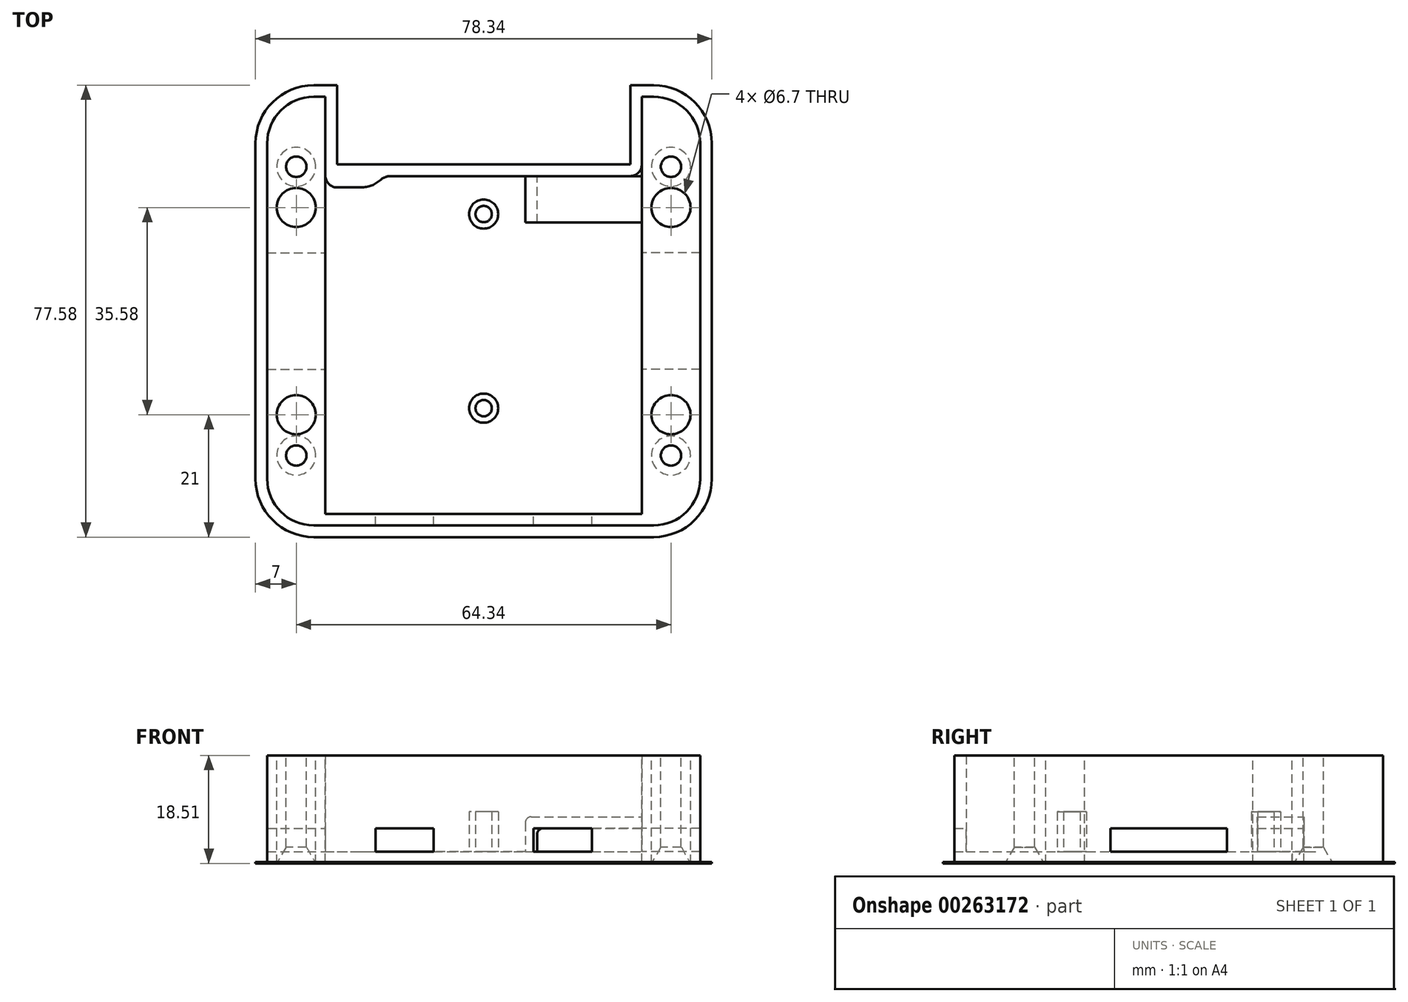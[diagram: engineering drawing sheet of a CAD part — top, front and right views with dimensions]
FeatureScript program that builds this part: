
annotation { "Feature Type Name" : "Feature", "Feature Type Description" : "" }
export const myFeature = defineFeature(function(context is Context, id is Id, definition is map)
    precondition{}
    {
        {
            var Q0;
            Q0=qCreatedBy(makeId("Top.planeOp"),FACE);
            var sketch = newSketch(context, id + "F0", { "sketchPlane" : qUnion([Q0])});
            skLineSegment(sketch, "E0.bottom", {"start": v(8, 0) * mm, "end": v(66.34, 0) * mm, "construction": true});
            skLineSegment(sketch, "E0.top", {"start": v(8, 73.58) * mm, "end": v(66.34, 73.58) * mm, "construction": true});
            skLineSegment(sketch, "E0.left", {"start": v(0, 8) * mm, "end": v(0, 65.58) * mm, "construction": true});
            skLineSegment(sketch, "E0.right", {"start": v(74.34, 8) * mm, "end": v(74.34, 65.58) * mm, "construction": true});
            skArc(sketch, "E1", {"start": v(8, 73.58) * mm, "mid": v(2.34, 71.24) * mm, "end": v(0, 65.58) * mm, "construction": true});
            skArc(sketch, "E2", {"start": v(0, 8) * mm, "mid": v(2.34, 2.34) * mm, "end": v(8, 0) * mm, "construction": true});
            skArc(sketch, "E3", {"start": v(74.34, 65.58) * mm, "mid": v(72, 71.24) * mm, "end": v(66.34, 73.58) * mm, "construction": true});
            skArc(sketch, "E4", {"start": v(66.34, 0) * mm, "mid": v(72, 2.34) * mm, "end": v(74.34, 8) * mm, "construction": true});
            skCircle(sketch, "E5", {"center": v(5, 61.58) * mm, "radius": 1.4 * mm, "construction": true});
            skCircle(sketch, "E6", {"center": v(5, 54.58) * mm, "radius": 3.35 * mm, "construction": true});
            skLineSegment(sketch, "E7", {"start": v(0, 36.8) * mm, "end": v(74.34, 36.8) * mm, "construction": true});
            skLineSegment(sketch, "E8", {"start": v(37.17, 73.58) * mm, "end": v(37.17, 0) * mm, "construction": true});
            skCircle(sketch, "E9.MirrorC", {"center": v(69.34, 54.58) * mm, "radius": 3.35 * mm, "construction": true});
            skCircle(sketch, "E10.MirrorC", {"center": v(69.34, 61.58) * mm, "radius": 1.4 * mm, "construction": true});
            skCircle(sketch, "E11.MirrorC", {"center": v(69.34, 12) * mm, "radius": 1.4 * mm, "construction": true});
            skCircle(sketch, "E12.MirrorC", {"center": v(69.34, 19) * mm, "radius": 3.35 * mm, "construction": true});
            skCircle(sketch, "E13.MirrorC", {"center": v(5, 19) * mm, "radius": 3.35 * mm, "construction": true});
            skCircle(sketch, "E14.MirrorC", {"center": v(5, 12) * mm, "radius": 1.4 * mm, "construction": true});
            skCircle(sketch, "E15", {"center": v(16.14, 63.03) * mm, "radius": 3.3 * mm, "construction": true});
            skLineSegment(sketch, "E16.bottom", {"start": v(10.83, 54.55) * mm, "end": v(15.24, 54.55) * mm, "construction": true});
            skLineSegment(sketch, "E16.top", {"start": v(10.84, 5.31) * mm, "end": v(15.25, 5.31) * mm, "construction": true});
            skLineSegment(sketch, "E16.left", {"start": v(10.83, 54.55) * mm, "end": v(10.83, 5.31) * mm, "construction": true});
            skLineSegment(sketch, "E16.right", {"start": v(15.24, 54.55) * mm, "end": v(15.24, 5.31) * mm, "construction": true});
            skLineSegment(sketch, "E17.bottom", {"start": v(32.84, 69.48) * mm, "end": v(62.84, 69.48) * mm, "construction": true});
            skLineSegment(sketch, "E17.top", {"start": v(32.84, 59.98) * mm, "end": v(62.84, 59.98) * mm, "construction": true});
            skLineSegment(sketch, "E17.left", {"start": v(32.84, 69.48) * mm, "end": v(32.84, 59.98) * mm, "construction": true});
            skLineSegment(sketch, "E17.right", {"start": v(62.84, 69.48) * mm, "end": v(62.84, 59.98) * mm, "construction": true});
            skLineSegment(sketch, "E18.bottom", {"start": v(59.1, 45.4) * mm, "end": v(63.5, 45.4) * mm, "construction": true});
            skLineSegment(sketch, "E18.top", {"start": v(59.1, 5.3) * mm, "end": v(63.5, 5.3) * mm, "construction": true});
            skLineSegment(sketch, "E18.left", {"start": v(59.1, 45.4) * mm, "end": v(59.1, 5.3) * mm, "construction": true});
            skLineSegment(sketch, "E18.right", {"start": v(63.5, 45.4) * mm, "end": v(63.5, 5.3) * mm, "construction": true});
            skLineSegment(sketch, "E19.bottom", {"start": v(19.88, 57) * mm, "end": v(31.88, 57) * mm, "construction": true});
            skLineSegment(sketch, "E19.top", {"start": v(19.88, 41) * mm, "end": v(21.13, 41) * mm, "construction": true});
            skLineSegment(sketch, "E19.left", {"start": v(19.88, 57) * mm, "end": v(19.88, 41) * mm, "construction": true});
            skLineSegment(sketch, "E19.right", {"start": v(31.88, 57) * mm, "end": v(31.88, 41) * mm, "construction": true});
            skLineSegment(sketch, "E20", {"start": v(21.13, 41) * mm, "end": v(21.14, 8.5) * mm, "construction": true});
            skLineSegment(sketch, "E21", {"start": v(21.14, 8.5) * mm, "end": v(30.64, 8.5) * mm, "construction": true});
            skLineSegment(sketch, "E22", {"start": v(30.64, 8.5) * mm, "end": v(30.64, 41) * mm, "construction": true});
            skLineSegment(sketch, "E23.trimOffspring", {"start": v(30.64, 41) * mm, "end": v(31.88, 41) * mm, "construction": true});
            skSolve(sketch);
        }
        {
            var Q0;
            Q0=qCreatedBy(makeId("Top.planeOp"),FACE);
            var sketch = newSketch(context, id + "F1", { "sketchPlane" : qUnion([Q0])});
            skLineSegment(sketch, "E24", {"start": v(0, 65.58) * mm, "end": v(0, 8) * mm});
            skLineSegment(sketch, "E25", {"start": v(74.34, 65.58) * mm, "end": v(74.34, 8) * mm});
            skCircle(sketch, "E26", {"center": v(5, 61.58) * mm, "radius": 1.75 * mm});
            skCircle(sketch, "E27", {"center": v(5, 12) * mm, "radius": 1.75 * mm});
            skCircle(sketch, "E28", {"center": v(69.34, 12) * mm, "radius": 1.75 * mm});
            skCircle(sketch, "E29", {"center": v(69.34, 61.58) * mm, "radius": 1.75 * mm});
            skCircle(sketch, "E30", {"center": v(5, 54.58) * mm, "radius": 3.35 * mm});
            skCircle(sketch, "E31", {"center": v(5, 19) * mm, "radius": 3.35 * mm});
            skCircle(sketch, "E32", {"center": v(69.34, 19) * mm, "radius": 3.35 * mm});
            skCircle(sketch, "E33", {"center": v(69.34, 54.58) * mm, "radius": 3.35 * mm});
            skLineSegment(sketch, "E34", {"start": v(8, 73.58) * mm, "end": v(10, 73.58) * mm});
            skArc(sketch, "E35", {"start": v(8, 73.58) * mm, "mid": v(2.34, 71.24) * mm, "end": v(0, 65.58) * mm});
            skArc(sketch, "E36", {"start": v(74.34, 65.58) * mm, "mid": v(72, 71.24) * mm, "end": v(66.34, 73.58) * mm});
            skLineSegment(sketch, "E37", {"start": v(8, 0) * mm, "end": v(66.34, 0) * mm});
            skArc(sketch, "E38", {"start": v(0, 8) * mm, "mid": v(2.34, 2.34) * mm, "end": v(8, 0) * mm});
            skArc(sketch, "E39", {"start": v(66.34, 0) * mm, "mid": v(72, 2.34) * mm, "end": v(74.34, 8) * mm});
            skArc(sketch, "E40", {"start": v(16.14, 58.03) * mm, "mid": v(17.94, 58.37) * mm, "end": v(19.5, 59.33) * mm});
            skLineSegment(sketch, "E41", {"start": v(64.34, 59.98) * mm, "end": v(21.18, 59.98) * mm});
            skArc(sketch, "E42", {"start": v(21.18, 59.98) * mm, "mid": v(20.28, 59.81) * mm, "end": v(19.5, 59.33) * mm});
            skLineSegment(sketch, "E43", {"start": v(64.34, 59.98) * mm, "end": v(64.34, 73.58) * mm});
            skLineSegment(sketch, "E44", {"start": v(66.34, 73.58) * mm, "end": v(64.34, 73.58) * mm});
            skLineSegment(sketch, "E45", {"start": v(10, 73.58) * mm, "end": v(10, 58.03) * mm});
            skLineSegment(sketch, "E46", {"start": v(10, 58.03) * mm, "end": v(16.14, 58.03) * mm});
            skSolve(sketch);
        }
        {
            var Q0;
            Q0=qSketchRegion(id+"F1",true);
            extrude(context, id + "F2", {"entities" : qUnion([Q0]), "oppositeDirection" : true, "depth" : 2 * mm});
        }
        {
            var Q0;
            Q0=makeQuery(id+"F2.opExtrude","SWEPT_EDGE",EDGE,{"disambiguationData":[OSD([sQuery(id+"F1.wireOp",EDGE,"E45"),sQuery(id+"F1.wireOp",EDGE,"E46")])]});
            var Q1;
            Q1=makeQuery(id+"F2.opExtrude","SWEPT_EDGE",EDGE,{"disambiguationData":[OSD([sQuery(id+"F1.wireOp",EDGE,"E41"),sQuery(id+"F1.wireOp",EDGE,"E43")])]});
            fillet(context, id + "F3", {"entities" : qUnion([Q0, Q1]), "radius" : 2 * mm, "tangentPropagation" : true, "allowEdgeOverflow" : false});
        }
        {
            var Q0;
            Q0=makeQuery(id+"F2.opExtrude","CAP_FACE",FACE,{"disambiguationData":[OSD([sQuery(id+"F1.wireOp",EDGE,"E24"),sQuery(id+"F1.wireOp",EDGE,"E25"),sQuery(id+"F1.wireOp",EDGE,"E26"),sQuery(id+"F1.wireOp",EDGE,"E27"),sQuery(id+"F1.wireOp",EDGE,"E28"),sQuery(id+"F1.wireOp",EDGE,"E29"),sQuery(id+"F1.wireOp",EDGE,"E30"),sQuery(id+"F1.wireOp",EDGE,"E31"),sQuery(id+"F1.wireOp",EDGE,"E32"),sQuery(id+"F1.wireOp",EDGE,"E33"),sQuery(id+"F1.wireOp",EDGE,"E34"),sQuery(id+"F1.wireOp",EDGE,"E35"),sQuery(id+"F1.wireOp",EDGE,"E36"),sQuery(id+"F1.wireOp",EDGE,"E37"),sQuery(id+"F1.wireOp",EDGE,"E38"),sQuery(id+"F1.wireOp",EDGE,"E39"),sQuery(id+"F1.wireOp",EDGE,"E40"),sQuery(id+"F1.wireOp",EDGE,"szp27tM4-Ggn2-58AR-YqNy-7nc7cWW06Emm"),sQuery(id+"F1.wireOp",EDGE,"0f7bfab5-27f3-44fa-b1d4-cae2101ceb6e.trimOffspring"),sQuery(id+"F1.wireOp",EDGE,"bU7Ev4i4-ZTTS-p5M7-DCLq-JKvuHiUkPX25"),sQuery(id+"F1.wireOp",EDGE,"E41"),sQuery(id+"F1.wireOp",EDGE,"E42")])],"isStart":true});
            var sketch = newSketch(context, id + "F4", { "sketchPlane" : qUnion([Q0])});
            skLineSegment(sketch, "E47", {"start": v(0, 65.58) * mm, "end": v(0, 8) * mm});
            skArc(sketch, "E48", {"start": v(0, 8) * mm, "mid": v(2.34, 2.34) * mm, "end": v(8, 0) * mm});
            skLineSegment(sketch, "E49", {"start": v(8, 0) * mm, "end": v(66.34, 0) * mm});
            skArc(sketch, "E50", {"start": v(66.34, 0) * mm, "mid": v(72, 2.34) * mm, "end": v(74.34, 8) * mm});
            skLineSegment(sketch, "E51", {"start": v(64.34, 73.58) * mm, "end": v(64.34, 2) * mm});
            skLineSegment(sketch, "E52", {"start": v(10, 2) * mm, "end": v(64.34, 2) * mm});
            skLineSegment(sketch, "E53", {"start": v(10, 2) * mm, "end": v(10, 73.58) * mm});
            skArc(sketch, "E54", {"start": v(8, 73.58) * mm, "mid": v(2.34, 71.24) * mm, "end": v(0, 65.58) * mm});
            skLineSegment(sketch, "E55", {"start": v(8, 73.58) * mm, "end": v(10, 73.58) * mm});
            skArc(sketch, "E56", {"start": v(74.34, 65.58) * mm, "mid": v(72, 71.24) * mm, "end": v(66.34, 73.58) * mm});
            skLineSegment(sketch, "E57", {"start": v(64.34, 73.58) * mm, "end": v(66.34, 73.58) * mm});
            skLineSegment(sketch, "E58", {"start": v(74.34, 65.58) * mm, "end": v(74.34, 8) * mm});
            skCircle(sketch, "E59", {"center": v(5, 61.58) * mm, "radius": 1.75 * mm});
            skCircle(sketch, "E60", {"center": v(5, 54.58) * mm, "radius": 3.35 * mm});
            skCircle(sketch, "E61", {"center": v(5, 19) * mm, "radius": 3.35 * mm});
            skCircle(sketch, "E62", {"center": v(5, 12) * mm, "radius": 1.75 * mm});
            skCircle(sketch, "E63", {"center": v(69.34, 12) * mm, "radius": 1.75 * mm});
            skCircle(sketch, "E64", {"center": v(69.34, 19) * mm, "radius": 3.35 * mm});
            skCircle(sketch, "E65", {"center": v(69.34, 61.58) * mm, "radius": 1.75 * mm});
            skCircle(sketch, "E66", {"center": v(69.34, 54.58) * mm, "radius": 3.35 * mm});
            skSolve(sketch);
        }
        {
            var Q0;
            Q0=qSketchRegion(id+"F4",true);
            extrude(context, id + "F5", {"entities" : qUnion([Q0]), "operationType" : NewBodyOperationType.ADD, "depth" : 16.51 * mm});
        }
        {
            var Q0;
            Q0=makeQuery(id+"F2.opExtrude","CAP_EDGE",EDGE,{"disambiguationData":[OSD([sQuery(id+"F1.wireOp",EDGE,"E26")])],"isStart":false});
            var Q1;
            Q1=makeQuery(id+"F2.opExtrude","CAP_EDGE",EDGE,{"disambiguationData":[OSD([sQuery(id+"F1.wireOp",EDGE,"E27")])],"isStart":false});
            var Q2;
            Q2=makeQuery(id+"F2.opExtrude","CAP_EDGE",EDGE,{"disambiguationData":[OSD([sQuery(id+"F1.wireOp",EDGE,"E28")])],"isStart":false});
            var Q3;
            Q3=makeQuery(id+"F2.opExtrude","CAP_EDGE",EDGE,{"disambiguationData":[OSD([sQuery(id+"F1.wireOp",EDGE,"E29")])],"isStart":false});
            chamfer(context, id + "F6", {"entities" : qUnion([Q0, Q1, Q2, Q3]), "chamferType" : ChamferType.TWO_OFFSETS, "width1" : 1.6 * mm, "oppositeDirection" : false, "width2" : 2.8 * mm, "tangentPropagation" : true});
        }
        {
            var Q0;
            Q0=makeQuery(id+"F2.opExtrude","CAP_FACE",FACE,{"disambiguationData":[OSD([sQuery(id+"F1.wireOp",EDGE,"E24"),sQuery(id+"F1.wireOp",EDGE,"E25"),sQuery(id+"F1.wireOp",EDGE,"E26"),sQuery(id+"F1.wireOp",EDGE,"E27"),sQuery(id+"F1.wireOp",EDGE,"E28"),sQuery(id+"F1.wireOp",EDGE,"E29"),sQuery(id+"F1.wireOp",EDGE,"E30"),sQuery(id+"F1.wireOp",EDGE,"E31"),sQuery(id+"F1.wireOp",EDGE,"E32"),sQuery(id+"F1.wireOp",EDGE,"E33"),sQuery(id+"F1.wireOp",EDGE,"E34"),sQuery(id+"F1.wireOp",EDGE,"E35"),sQuery(id+"F1.wireOp",EDGE,"E36"),sQuery(id+"F1.wireOp",EDGE,"E37"),sQuery(id+"F1.wireOp",EDGE,"E38"),sQuery(id+"F1.wireOp",EDGE,"E39"),sQuery(id+"F1.wireOp",EDGE,"E40"),sQuery(id+"F1.wireOp",EDGE,"E41"),sQuery(id+"F1.wireOp",EDGE,"E42"),sQuery(id+"F1.wireOp",EDGE,"E43"),sQuery(id+"F1.wireOp",EDGE,"E44"),sQuery(id+"F1.wireOp",EDGE,"E45"),sQuery(id+"F1.wireOp",EDGE,"E46")])],"isStart":true});
            var sketch = newSketch(context, id + "F7", { "sketchPlane" : qUnion([Q0])});
            skLineSegment(sketch, "E67.bottom", {"start": v(31.67, 49.45) * mm, "end": v(42.67, 49.45) * mm, "construction": true});
            skLineSegment(sketch, "E67.top", {"start": v(31.67, 24.13) * mm, "end": v(42.67, 24.13) * mm, "construction": true});
            skLineSegment(sketch, "E67.left", {"start": v(31.67, 49.45) * mm, "end": v(31.67, 24.13) * mm, "construction": true});
            skLineSegment(sketch, "E67.right", {"start": v(42.67, 49.45) * mm, "end": v(42.67, 24.13) * mm, "construction": true});
            skCircle(sketch, "E68", {"center": v(37.17, 53.45) * mm, "radius": 2.5 * mm});
            skCircle(sketch, "E69", {"center": v(37.17, 20.13) * mm, "radius": 2.5 * mm});
            skCircle(sketch, "E70", {"center": v(37.17, 53.45) * mm, "radius": 1.4 * mm});
            skCircle(sketch, "E71", {"center": v(37.17, 20.13) * mm, "radius": 1.4 * mm});
            skSolve(sketch);
        }
        {
            var Q0;
            Q0=qSketchRegion(id+"F7",true);
            extrude(context, id + "F8", {"entities" : qUnion([Q0]), "operationType" : NewBodyOperationType.ADD, "depth" : 6.85 * mm});
        }
        {
            var Q0;
            Q0=makeQuery(id+"F5.boolean.opBoolean","MERGE",FACE,{"derivedFrom":[makeQuery(id+"F2.opExtrude","SWEPT_FACE",FACE,{"disambiguationData":[OSD([sQuery(id+"F1.wireOp",EDGE,"E45")])]}),makeQuery(id+"F5.opExtrude","SWEPT_FACE",FACE,{"disambiguationData":[OSD([sQuery(id+"F4.wireOp",EDGE,"E53")])]})]});
            var sketch = newSketch(context, id + "F9", { "sketchPlane" : qUnion([Q0])});
            skLineSegment(sketch, "E72.bottom", {"start": v(26.8, 4) * mm, "end": v(46.8, 4) * mm});
            skLineSegment(sketch, "E72.top", {"start": v(26.8, 0) * mm, "end": v(46.8, 0) * mm});
            skLineSegment(sketch, "E72.left", {"start": v(26.8, 4) * mm, "end": v(26.8, 0) * mm});
            skLineSegment(sketch, "E72.right", {"start": v(46.8, 4) * mm, "end": v(46.8, 0) * mm});
            skLineSegment(sketch, "E73", {"start": v(36.8, 4) * mm, "end": v(36.8, 0) * mm, "construction": true});
            skSolve(sketch);
        }
        {
            var Q0;
            Q0=qSketchRegion(id+"F9",true);
            extrude(context, id + "F10", {"entities" : qUnion([Q0]), "operationType" : NewBodyOperationType.REMOVE, "endBound" : BoundingType.THROUGH_ALL, "oppositeDirection" : true, "depth" : 25 * mm});
        }
        {
            var Q0;
            Q0=makeQuery(id+"F5.boolean.opBoolean","MERGE",FACE,{"derivedFrom":[makeQuery(id+"F2.opExtrude","SWEPT_FACE",FACE,{"disambiguationData":[OSD([sQuery(id+"F1.wireOp",EDGE,"E43")])]}),makeQuery(id+"F5.opExtrude","SWEPT_FACE",FACE,{"disambiguationData":[OSD([sQuery(id+"F4.wireOp",EDGE,"E51")])]})]});
            var sketch = newSketch(context, id + "F11", { "sketchPlane" : qUnion([Q0])});
            skLineSegment(sketch, "E74.bottom", {"start": v(-46.79, 0) * mm, "end": v(-26.79, 0) * mm});
            skLineSegment(sketch, "E74.top", {"start": v(-46.79, 4) * mm, "end": v(-26.79, 4) * mm});
            skLineSegment(sketch, "E74.left", {"start": v(-46.79, 0) * mm, "end": v(-46.79, 4) * mm});
            skLineSegment(sketch, "E74.right", {"start": v(-26.79, 0) * mm, "end": v(-26.79, 4) * mm});
            skLineSegment(sketch, "E75", {"start": v(-36.79, 4) * mm, "end": v(-36.79, 0) * mm, "construction": true});
            skSolve(sketch);
        }
        {
            var Q0;
            Q0=qSketchRegion(id+"F11",true);
            extrude(context, id + "F12", {"entities" : qUnion([Q0]), "operationType" : NewBodyOperationType.REMOVE, "endBound" : BoundingType.THROUGH_ALL, "oppositeDirection" : true, "depth" : 25 * mm});
        }
        {
            var Q0;
            Q0=makeQuery(id+"F5.opExtrude","SWEPT_FACE",FACE,{"disambiguationData":[OSD([sQuery(id+"F4.wireOp",EDGE,"E52")])]});
            var sketch = newSketch(context, id + "F13", { "sketchPlane" : qUnion([Q0])});
            skLineSegment(sketch, "E76", {"start": v(-37.17, 16.51) * mm, "end": v(-37.17, 0) * mm, "construction": true});
            skLineSegment(sketch, "E77.bottom", {"start": v(-55.76, 0) * mm, "end": v(-45.76, 0) * mm});
            skLineSegment(sketch, "E77.top", {"start": v(-55.76, 4) * mm, "end": v(-45.76, 4) * mm});
            skLineSegment(sketch, "E77.left", {"start": v(-55.76, 0) * mm, "end": v(-55.76, 4) * mm});
            skLineSegment(sketch, "E77.right", {"start": v(-45.76, 0) * mm, "end": v(-45.76, 4) * mm});
            skLineSegment(sketch, "E78.MirrorCS", {"start": v(-28.59, 0) * mm, "end": v(-28.59, 4) * mm});
            skLineSegment(sketch, "E79.MirrorCS", {"start": v(-18.59, 0) * mm, "end": v(-18.59, 4) * mm});
            skLineSegment(sketch, "E80.MirrorCS", {"start": v(-18.59, 4) * mm, "end": v(-28.59, 4) * mm});
            skLineSegment(sketch, "E81.MirrorCS", {"start": v(-18.59, 0) * mm, "end": v(-28.59, 0) * mm});
            skSolve(sketch);
        }
        {
            var Q0;
            Q0=qSketchRegion(id+"F13",true);
            extrude(context, id + "F14", {"entities" : qUnion([Q0]), "operationType" : NewBodyOperationType.REMOVE, "endBound" : BoundingType.THROUGH_ALL, "oppositeDirection" : true, "depth" : 25 * mm});
        }
        {
            var Q0;
            {var subQ0=sQuery(id+"F1.wireOp",EDGE,"E41");var subQ1=sQuery(id+"F1.wireOp",EDGE,"E46");var subQ2=sQuery(id+"F1.wireOp",EDGE,"E45");var subQ3=sQuery(id+"F1.wireOp",EDGE,"E43");var subQ4=sQuery(id+"F1.wireOp",EDGE,"E42");var subQ5=sQuery(id+"F1.wireOp",EDGE,"E40");Q0=makeQuery(id+"F14.boolean.opBoolean","MERGE",FACE,{"derivedFrom":[makeQuery(id+"F12.boolean.opBoolean","MERGE",FACE,{"derivedFrom":[makeQuery(id+"F10.boolean.opBoolean","MERGE",FACE,{"derivedFrom":[makeQuery(id+"F8.boolean.opBoolean","SPLIT",FACE,{"disambiguationData":[TD([makeQuery(id+"F2.opExtrude","SWEPT_FACE",FACE,{"disambiguationData":[OSD([subQ5])]})])],"derivedFrom":makeQuery(id+"F2.opExtrude","CAP_FACE",FACE,{"disambiguationData":[OSD([sQuery(id+"F1.wireOp",EDGE,"E24"),sQuery(id+"F1.wireOp",EDGE,"E25"),sQuery(id+"F1.wireOp",EDGE,"E26"),sQuery(id+"F1.wireOp",EDGE,"E27"),sQuery(id+"F1.wireOp",EDGE,"E28"),sQuery(id+"F1.wireOp",EDGE,"E29"),sQuery(id+"F1.wireOp",EDGE,"E30"),sQuery(id+"F1.wireOp",EDGE,"E31"),sQuery(id+"F1.wireOp",EDGE,"E32"),sQuery(id+"F1.wireOp",EDGE,"E33"),sQuery(id+"F1.wireOp",EDGE,"E34"),sQuery(id+"F1.wireOp",EDGE,"E35"),sQuery(id+"F1.wireOp",EDGE,"E36"),sQuery(id+"F1.wireOp",EDGE,"E37"),sQuery(id+"F1.wireOp",EDGE,"E38"),sQuery(id+"F1.wireOp",EDGE,"E39"),subQ5,subQ0,subQ4,subQ3,sQuery(id+"F1.wireOp",EDGE,"E44"),subQ2,subQ1])],"isStart":true})}),makeQuery(id+"F10.opExtrude","SWEPT_FACE",FACE,{"disambiguationData":[OSD([sQuery(id+"F9.wireOp",EDGE,"E72.top")])]})]}),makeQuery(id+"F12.opExtrude","SWEPT_FACE",FACE,{"disambiguationData":[OSD([sQuery(id+"F11.wireOp",EDGE,"E74.bottom")])]})]}),makeQuery(id+"F14.opExtrude","SWEPT_FACE",FACE,{"disambiguationData":[OSD([sQuery(id+"F13.wireOp",EDGE,"E77.bottom")])]}),makeQuery(id+"F14.opExtrude","SWEPT_FACE",FACE,{"disambiguationData":[OSD([sQuery(id+"F13.wireOp",EDGE,"E81.MirrorCS")])]})]});}
            var sketch = newSketch(context, id + "F15", { "sketchPlane" : qUnion([Q0])});
            skLineSegment(sketch, "E82.bottom", {"start": v(44.34, 59.98) * mm, "end": v(64.34, 59.98) * mm});
            skLineSegment(sketch, "E82.top", {"start": v(44.34, 51.98) * mm, "end": v(64.34, 51.98) * mm});
            skLineSegment(sketch, "E82.left", {"start": v(44.34, 59.98) * mm, "end": v(44.34, 51.98) * mm});
            skLineSegment(sketch, "E82.right", {"start": v(64.34, 59.98) * mm, "end": v(64.34, 51.98) * mm});
            skSolve(sketch);
        }
        {
            var Q0;
            Q0=qSketchRegion(id+"F15",true);
            extrude(context, id + "F16", {"entities" : qUnion([Q0]), "operationType" : NewBodyOperationType.ADD, "depth" : 6 * mm});
        }
        {
            var Q0;
            Q0=makeQuery(id+"F16.boolean.opBoolean","MERGE",FACE,{"derivedFrom":[makeQuery(id+"F2.opExtrude","SWEPT_FACE",FACE,{"disambiguationData":[OSD([sQuery(id+"F1.wireOp",EDGE,"E41")])]}),makeQuery(id+"F16.opExtrude","SWEPT_FACE",FACE,{"disambiguationData":[OSD([sQuery(id+"F15.wireOp",EDGE,"E82.bottom")])]})]});
            var sketch = newSketch(context, id + "F17", { "sketchPlane" : qUnion([Q0])});
            skLineSegment(sketch, "E83.bottom", {"start": v(-64.34, 0) * mm, "end": v(-46.34, 0) * mm});
            skLineSegment(sketch, "E83.top", {"start": v(-64.34, 4) * mm, "end": v(-46.34, 4) * mm});
            skLineSegment(sketch, "E83.left", {"start": v(-64.34, 0) * mm, "end": v(-64.34, 4) * mm});
            skLineSegment(sketch, "E83.right", {"start": v(-46.34, 0) * mm, "end": v(-46.34, 4) * mm});
            skSolve(sketch);
        }
        {
            var Q0;
            Q0=qSketchRegion(id+"F17",true);
            var Q1;
            Q1=makeQuery(id+"F16.opExtrude","SWEPT_FACE",FACE,{"disambiguationData":[OSD([sQuery(id+"F15.wireOp",EDGE,"E82.top")])]});
            extrude(context, id + "F18", {"entities" : qUnion([Q0]), "operationType" : NewBodyOperationType.REMOVE, "endBound" : BoundingType.UP_TO_SURFACE, "oppositeDirection" : true, "endBoundEntityFace" : qUnion([Q1]), "depth" : 25 * mm});
        }
        {
            var Q0;
            Q0=makeQuery(id+"F18.boolean.opBoolean","COPY",EDGE,{"derivedFrom":makeQuery(id+"F18.opExtrude","SWEPT_EDGE",EDGE,{"disambiguationData":[OSD([sQuery(id+"F17.wireOp",EDGE,"E83.top"),sQuery(id+"F17.wireOp",EDGE,"E83.right")])]})});
            var Q1;
            Q1=makeQuery(id+"F16.opExtrude","CAP_EDGE",EDGE,{"disambiguationData":[OSD([sQuery(id+"F15.wireOp",EDGE,"E82.left")])],"isStart":false});
            fillet(context, id + "F19", {"entities" : qUnion([Q0, Q1]), "radius" : 1 * mm, "tangentPropagation" : true, "allowEdgeOverflow" : false});
        }
        {
            var Q0;
            Q0=makeQuery(id+"F2.opExtrude","CAP_FACE",FACE,{"disambiguationData":[OSD([sQuery(id+"F1.wireOp",EDGE,"E24"),sQuery(id+"F1.wireOp",EDGE,"E25"),sQuery(id+"F1.wireOp",EDGE,"E26"),sQuery(id+"F1.wireOp",EDGE,"E27"),sQuery(id+"F1.wireOp",EDGE,"E28"),sQuery(id+"F1.wireOp",EDGE,"E29"),sQuery(id+"F1.wireOp",EDGE,"E30"),sQuery(id+"F1.wireOp",EDGE,"E31"),sQuery(id+"F1.wireOp",EDGE,"E32"),sQuery(id+"F1.wireOp",EDGE,"E33"),sQuery(id+"F1.wireOp",EDGE,"E34"),sQuery(id+"F1.wireOp",EDGE,"E35"),sQuery(id+"F1.wireOp",EDGE,"E36"),sQuery(id+"F1.wireOp",EDGE,"E37"),sQuery(id+"F1.wireOp",EDGE,"E38"),sQuery(id+"F1.wireOp",EDGE,"E39"),sQuery(id+"F1.wireOp",EDGE,"E40"),sQuery(id+"F1.wireOp",EDGE,"E41"),sQuery(id+"F1.wireOp",EDGE,"E42"),sQuery(id+"F1.wireOp",EDGE,"E43"),sQuery(id+"F1.wireOp",EDGE,"E44"),sQuery(id+"F1.wireOp",EDGE,"E45"),sQuery(id+"F1.wireOp",EDGE,"E46")])],"isStart":false});
            var sketch = newSketch(context, id + "F20", { "sketchPlane" : qUnion([Q0])});
            skLineSegment(sketch, "E84", {"start": v(0, -8) * mm, "end": v(0, -65.58) * mm});
            skLineSegment(sketch, "E85", {"start": v(8, 0) * mm, "end": v(66.34, 0) * mm});
            skLineSegment(sketch, "E86", {"start": v(74.34, -8) * mm, "end": v(74.34, -65.58) * mm});
            skArc(sketch, "E87", {"start": v(8, 0) * mm, "mid": v(2.34, -2.34) * mm, "end": v(0, -8) * mm});
            skArc(sketch, "E88", {"start": v(74.34, -8) * mm, "mid": v(72, -2.34) * mm, "end": v(66.34, 0) * mm});
            skArc(sketch, "E89", {"start": v(66.34, -73.58) * mm, "mid": v(72, -71.24) * mm, "end": v(74.34, -65.58) * mm});
            skArc(sketch, "E90", {"start": v(0, -65.58) * mm, "mid": v(2.34, -71.24) * mm, "end": v(8, -73.58) * mm});
            skLineSegment(sketch, "E91", {"start": v(8, -73.58) * mm, "end": v(10, -73.58) * mm});
            skLineSegment(sketch, "E92", {"start": v(10, -73.58) * mm, "end": v(10, -60.03) * mm});
            skArc(sketch, "E93", {"start": v(12, -58.03) * mm, "mid": v(10.59, -58.62) * mm, "end": v(10, -60.03) * mm});
            skLineSegment(sketch, "E94", {"start": v(12, -58.03) * mm, "end": v(16.14, -58.03) * mm});
            skArc(sketch, "E95", {"start": v(19.5, -59.33) * mm, "mid": v(17.94, -58.37) * mm, "end": v(16.14, -58.03) * mm});
            skArc(sketch, "E96", {"start": v(19.5, -59.33) * mm, "mid": v(20.28, -59.81) * mm, "end": v(21.18, -59.98) * mm});
            skLineSegment(sketch, "E97", {"start": v(21.18, -59.98) * mm, "end": v(62.34, -59.98) * mm});
            skArc(sketch, "E98", {"start": v(64.34, -61.98) * mm, "mid": v(63.75, -60.57) * mm, "end": v(62.34, -59.98) * mm});
            skLineSegment(sketch, "E99", {"start": v(64.34, -61.98) * mm, "end": v(64.34, -73.58) * mm});
            skLineSegment(sketch, "E100", {"start": v(64.34, -73.58) * mm, "end": v(66.34, -73.58) * mm});
            skLineSegment(sketch, "E101", {"start": v(-2, -8) * mm, "end": v(-2, -65.58) * mm});
            skLineSegment(sketch, "E102", {"start": v(8, 2) * mm, "end": v(66.34, 2) * mm});
            skLineSegment(sketch, "E103", {"start": v(76.34, -8) * mm, "end": v(76.34, -65.58) * mm});
            skLineSegment(sketch, "E104", {"start": v(12, -61.98) * mm, "end": v(62.34, -61.98) * mm});
            skArc(sketch, "E105", {"start": v(8, 2) * mm, "mid": v(0.93, -0.93) * mm, "end": v(-2, -8) * mm});
            skArc(sketch, "E106", {"start": v(76.34, -8) * mm, "mid": v(73.41, -0.93) * mm, "end": v(66.34, 2) * mm});
            skArc(sketch, "E107", {"start": v(66.34, -75.58) * mm, "mid": v(73.41, -72.65) * mm, "end": v(76.34, -65.58) * mm});
            skLineSegment(sketch, "E108", {"start": v(62.34, -61.98) * mm, "end": v(62.34, -75.58) * mm});
            skLineSegment(sketch, "E109", {"start": v(66.34, -75.58) * mm, "end": v(62.34, -75.58) * mm});
            skLineSegment(sketch, "E110", {"start": v(12, -61.98) * mm, "end": v(12, -75.58) * mm});
            skLineSegment(sketch, "E111", {"start": v(12, -75.58) * mm, "end": v(8, -75.58) * mm});
            skArc(sketch, "E112", {"start": v(-2, -65.58) * mm, "mid": v(0.93, -72.65) * mm, "end": v(8, -75.58) * mm});
            skSolve(sketch);
        }
        {
            var Q0;
            Q0 = qSketchRegion(id + "F20", true);
            extrude(context, id + "F21", {"entities" : qUnion([Q0]), "operationType" : NewBodyOperationType.ADD, "oppositeDirection" : true, "depth" : 0.2 * mm});
        }
    });
